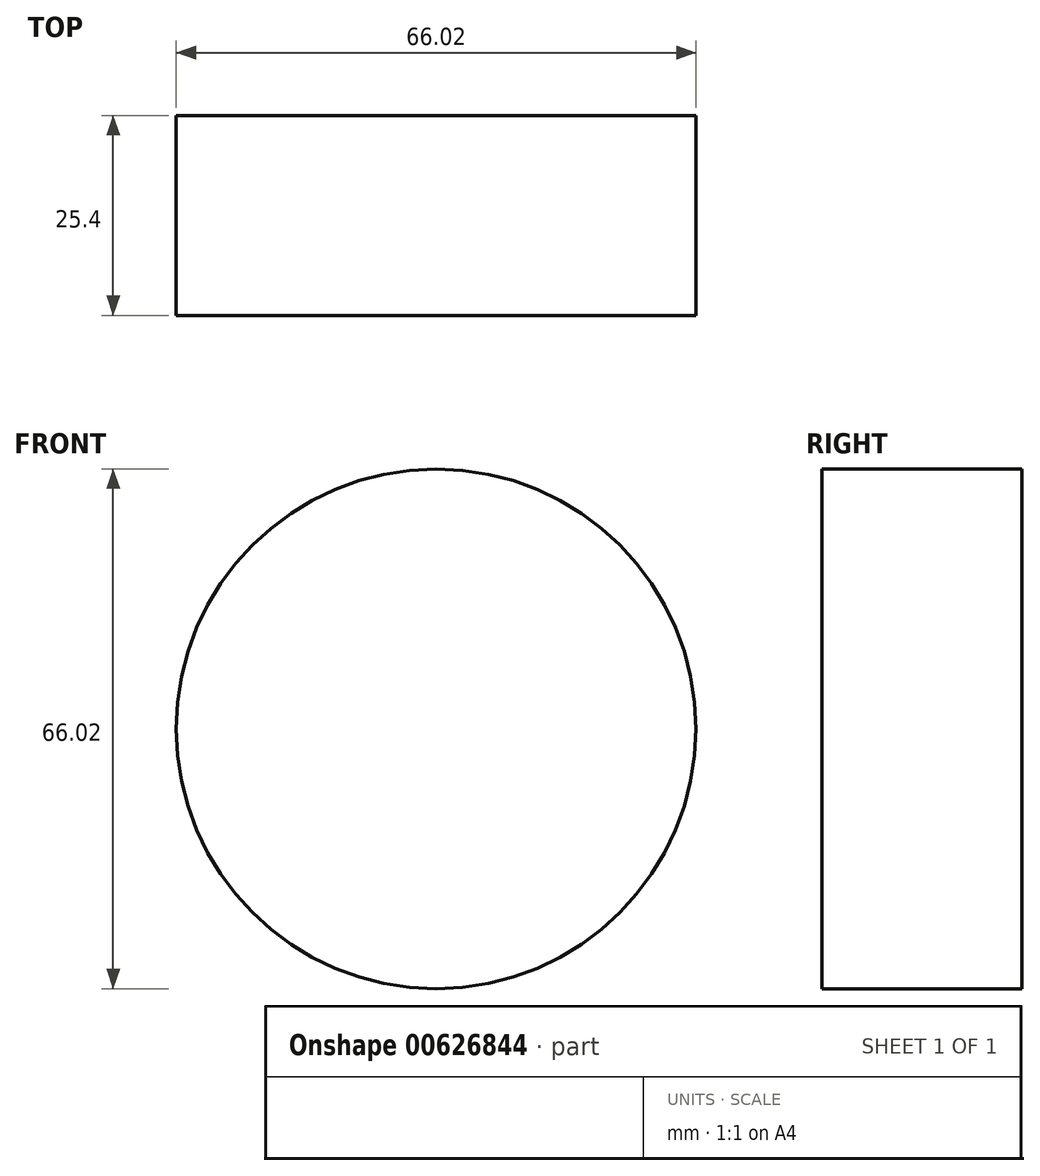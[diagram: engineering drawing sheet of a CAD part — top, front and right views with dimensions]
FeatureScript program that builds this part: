
annotation { "Feature Type Name" : "Feature", "Feature Type Description" : "" }
export const myFeature = defineFeature(function(context is Context, id is Id, definition is map)
    precondition{}
    {
        {
            var Q0;
            Q0=qCreatedBy(makeId("Front.planeOp"),FACE);
            var sketch = newSketch(context, id + "F0", { "sketchPlane" : qUnion([Q0])});
            skCircle(sketch, "E0", {"center": v(10.99, 0) * mm, "radius": 33 * mm});
            skSolve(sketch);
        }
        {
            var Q0;
            Q0 = qSketchRegion(id + "F0", true);
            extrude(context, id + "F1", {"entities" : qUnion([Q0]), "depth" : 25.4 * mm, "offsetDistance" : 25.4 * mm});
        }
    });
